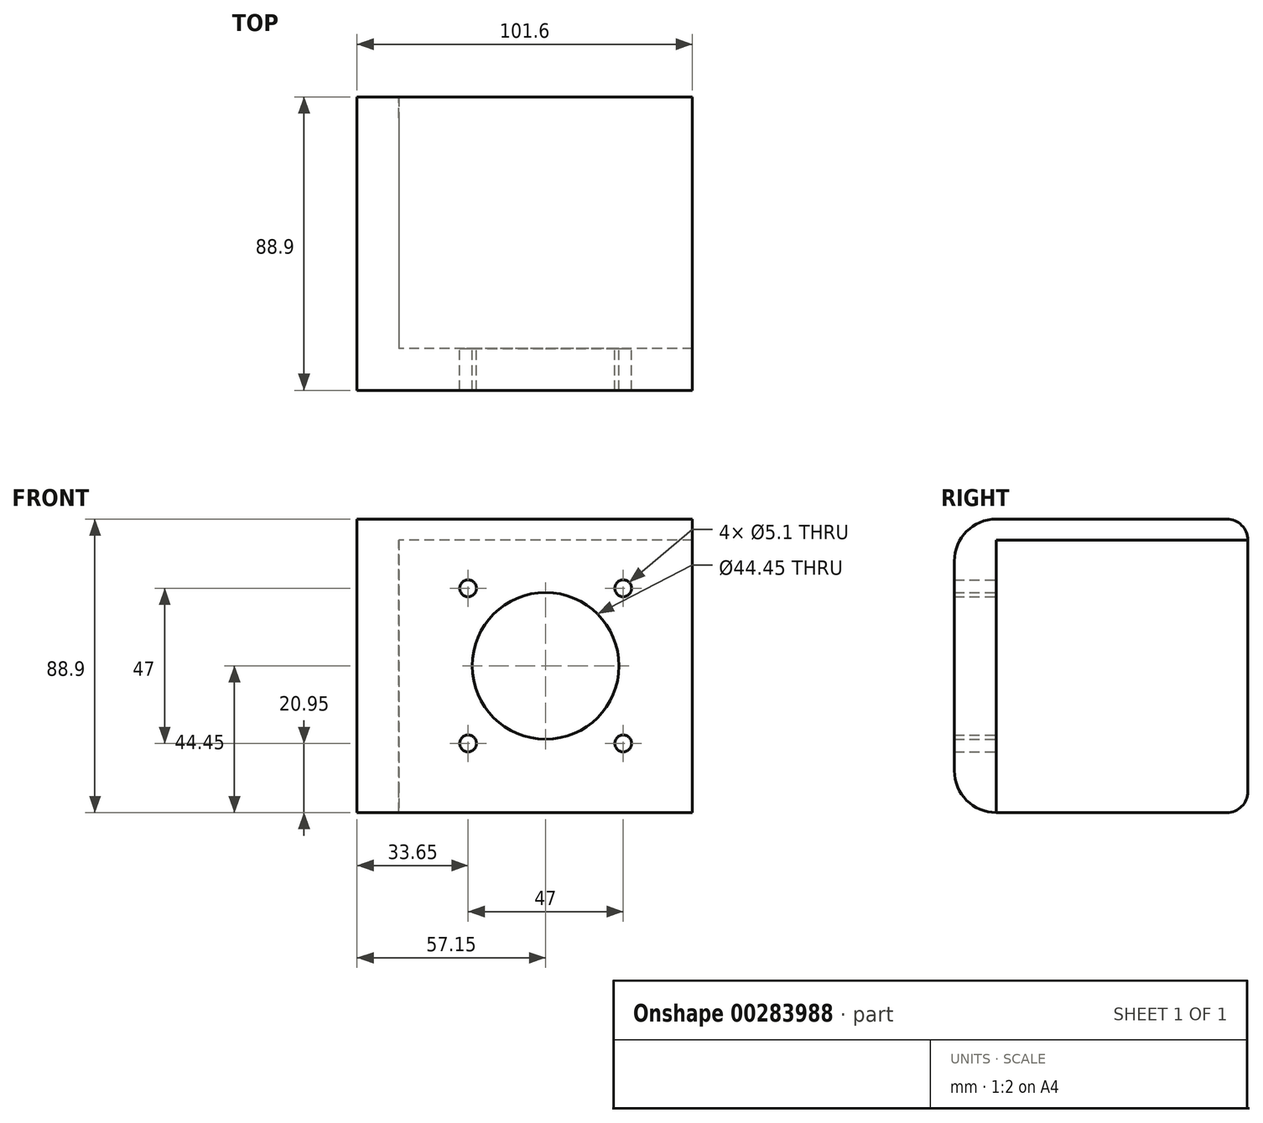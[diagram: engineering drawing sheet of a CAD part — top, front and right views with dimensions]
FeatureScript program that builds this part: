
annotation { "Feature Type Name" : "Feature", "Feature Type Description" : "" }
export const myFeature = defineFeature(function(context is Context, id is Id, definition is map)
    precondition{}
    {
        {
            var Q0;
            Q0=qCreatedBy(makeId("Right.planeOp"),FACE);
            var sketch = newSketch(context, id + "F0", { "sketchPlane" : qUnion([Q0])});
            skLineSegment(sketch, "E0.bottom", {"start": v(38.1, -44.45) * mm, "end": v(-31.75, -44.45) * mm});
            skLineSegment(sketch, "E0.top", {"start": v(38.1, 44.45) * mm, "end": v(-31.75, 44.45) * mm});
            skLineSegment(sketch, "E0.left", {"start": v(44.45, -38.1) * mm, "end": v(44.45, 38.1) * mm});
            skLineSegment(sketch, "E0.right", {"start": v(-44.45, -31.75) * mm, "end": v(-44.45, 31.75) * mm});
            skPoint(sketch, "E0.middle", {"position": v(0, 0) * mm});
            skPoint(sketch, "E1.visualSharp", {"position": v(-44.45, 44.45) * mm});
            skArc(sketch, "E1.filletArc", {"start": v(-31.75, 44.45) * mm, "mid": v(-40.73, 40.73) * mm, "end": v(-44.45, 31.75) * mm});
            skPoint(sketch, "E2.visualSharp", {"position": v(44.45, 44.45) * mm});
            skArc(sketch, "E2.filletArc", {"start": v(44.45, 38.1) * mm, "mid": v(42.6, 42.6) * mm, "end": v(38.1, 44.45) * mm});
            skPoint(sketch, "E3.visualSharp", {"position": v(44.45, -44.45) * mm});
            skArc(sketch, "E3.filletArc", {"start": v(38.1, -44.45) * mm, "mid": v(42.6, -42.6) * mm, "end": v(44.45, -38.1) * mm});
            skPoint(sketch, "E4.visualSharp", {"position": v(-44.45, -44.45) * mm});
            skArc(sketch, "E4.filletArc", {"start": v(-44.45, -31.75) * mm, "mid": v(-40.73, -40.73) * mm, "end": v(-31.75, -44.45) * mm});
            skLineSegment(sketch, "E5", {"start": v(-31.75, 44.45) * mm, "end": v(-31.75, -44.45) * mm});
            skLineSegment(sketch, "E6", {"start": v(44.45, 38.1) * mm, "end": v(-31.75, 38.1) * mm});
            skSolve(sketch);
        }
        {
            var Q0;
            Q0=makeQuery(id+"F0.imprint","IMPRINT",FACE,{"disambiguationData":[TD([[makeQuery(id+"F0.imprint","IMPRINT",EDGE,{"derivedFrom":sQuery(id+"F0.wireOp",EDGE,"E0.right")}),-1.0]])]});
            extrude(context, id + "F1", {"entities" : qUnion([Q0]), "depth" : 101.6 * mm});
        }
        {
            var Q0;
            Q0=makeQuery(id+"F0.imprint","IMPRINT",FACE,{"disambiguationData":[TD([[makeQuery(id+"F0.imprint","IMPRINT",EDGE,{"derivedFrom":sQuery(id+"F0.wireOp",EDGE,"E0.bottom")}),-1.0]])]});
            extrude(context, id + "F2", {"entities" : qUnion([Q0]), "operationType" : NewBodyOperationType.ADD, "depth" : 12.7 * mm});
        }
        {
            var Q0;
            Q0=makeQuery(id+"F1.opExtrude","SWEPT_FACE",FACE,{"disambiguationData":[OSD([sQuery(id+"F0.wireOp",EDGE,"E5")])]});
            var sketch = newSketch(context, id + "F3", { "sketchPlane" : qUnion([Q0])});
            skCircle(sketch, "E7", {"center": v(-57.15, 0) * mm, "radius": 22.23 * mm});
            skCircle(sketch, "E8", {"center": v(-33.65, 23.5) * mm, "radius": 2.55 * mm});
            skCircle(sketch, "E9.0.1.0", {"center": v(-33.65, -23.5) * mm, "radius": 2.55 * mm});
            skCircle(sketch, "E9.1.0.0", {"center": v(-80.65, 23.5) * mm, "radius": 2.55 * mm});
            skCircle(sketch, "E9.1.1.0", {"center": v(-80.65, -23.5) * mm, "radius": 2.55 * mm});
            skLineSegment(sketch, "E9.direction1", {"start": v(-33.65, 23.5) * mm, "end": v(-80.65, 23.5) * mm, "construction": true});
            skLineSegment(sketch, "E9.direction2", {"start": v(-33.65, 23.5) * mm, "end": v(-33.65, -23.5) * mm, "construction": true});
            skSolve(sketch);
        }
        {
            var Q0;
            Q0=makeQuery(id+"F3.imprint","IMPRINT",FACE,{"disambiguationData":[TD([[makeQuery(id+"F3.imprint","IMPRINT",EDGE,{"derivedFrom":sQuery(id+"F3.wireOp",EDGE,"E7")}),1.0]])]});
            var Q1;
            Q1=makeQuery(id+"F3.imprint","IMPRINT",FACE,{"disambiguationData":[TD([[makeQuery(id+"F3.imprint","IMPRINT",EDGE,{"derivedFrom":sQuery(id+"F3.wireOp",EDGE,"E9.0.1.0")}),1.0]])]});
            var Q2;
            Q2=makeQuery(id+"F3.imprint","IMPRINT",FACE,{"disambiguationData":[TD([[makeQuery(id+"F3.imprint","IMPRINT",EDGE,{"derivedFrom":sQuery(id+"F3.wireOp",EDGE,"E9.1.1.0")}),1.0]])]});
            var Q3;
            Q3=makeQuery(id+"F3.imprint","IMPRINT",FACE,{"disambiguationData":[TD([[makeQuery(id+"F3.imprint","IMPRINT",EDGE,{"derivedFrom":sQuery(id+"F3.wireOp",EDGE,"E9.1.0.0")}),1.0]])]});
            var Q4;
            Q4=makeQuery(id+"F3.imprint","IMPRINT",FACE,{"disambiguationData":[TD([[makeQuery(id+"F3.imprint","IMPRINT",EDGE,{"derivedFrom":sQuery(id+"F3.wireOp",EDGE,"E8")}),1.0]])]});
            extrude(context, id + "F4", {"entities" : qUnion([Q0, Q1, Q2, Q3, Q4]), "operationType" : NewBodyOperationType.REMOVE, "endBound" : BoundingType.THROUGH_ALL, "oppositeDirection" : true, "depth" : 25.4 * mm});
        }
        {
            var Q0;
            {var subQ0=sQuery(id+"F0.wireOp",EDGE,"E0.top");Q0=makeQuery(id+"F0.imprint","IMPRINT",FACE,{"disambiguationData":[TD([[makeQuery(id+"F0.imprint","IMPRINT",EDGE,{"derivedFrom":subQ0}),1.0]])]});}
            extrude(context, id + "F5", {"entities" : qUnion([Q0]), "operationType" : NewBodyOperationType.ADD, "depth" : 101.6 * mm});
        }
    });
